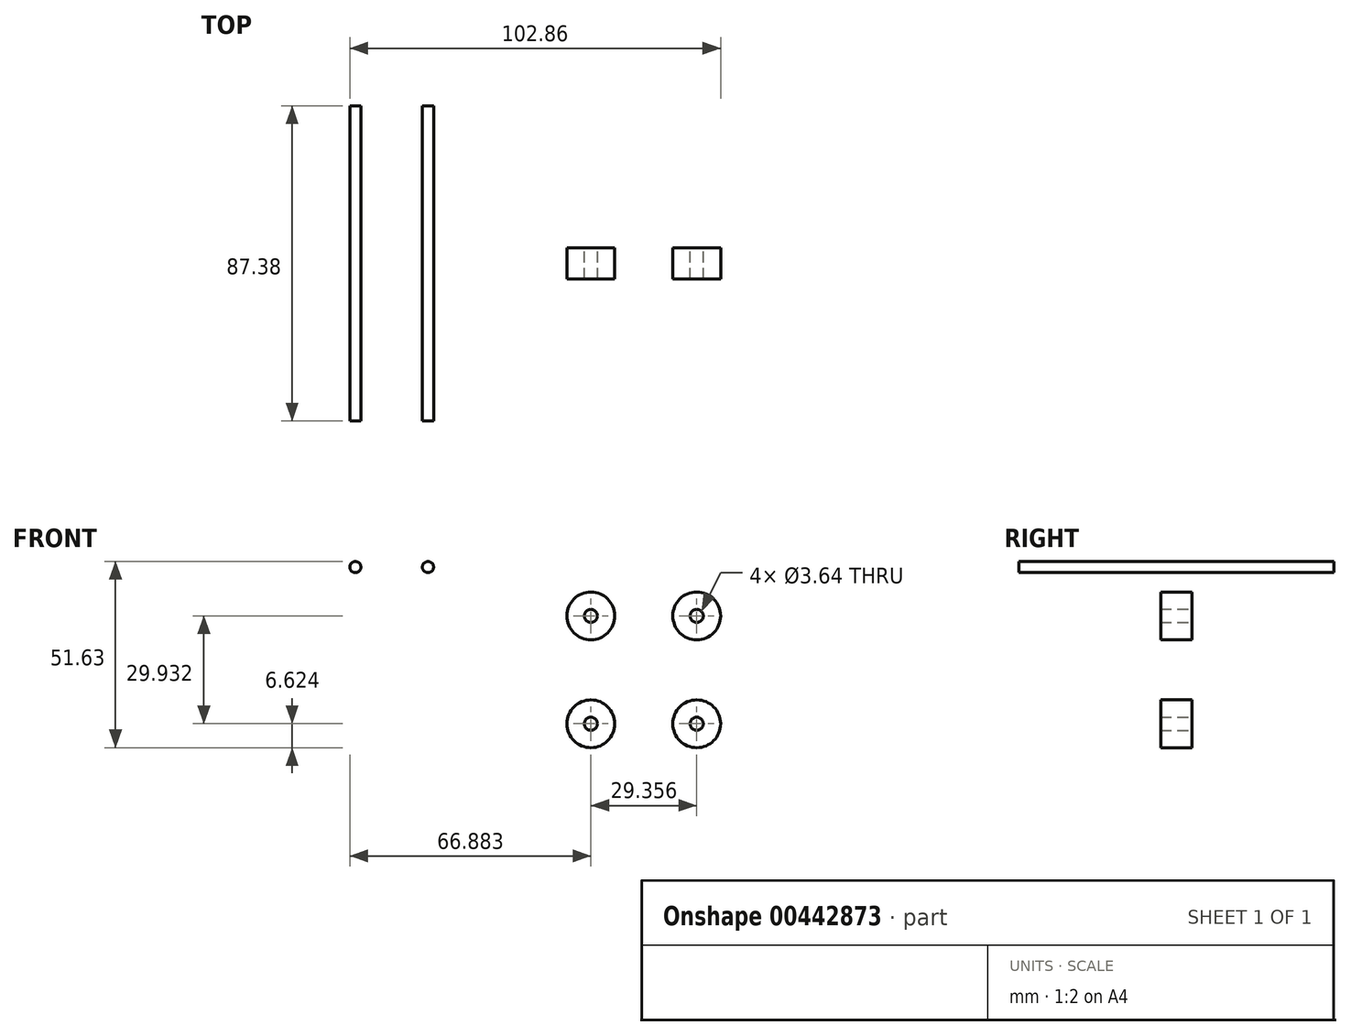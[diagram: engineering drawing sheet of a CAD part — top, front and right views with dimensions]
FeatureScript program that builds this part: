
annotation { "Feature Type Name" : "Feature", "Feature Type Description" : "" }
export const myFeature = defineFeature(function(context is Context, id is Id, definition is map)
    precondition{}
    {
        {
            var Q0;
            Q0=qCreatedBy(makeId("Front.planeOp"),FACE);
            var sketch = newSketch(context, id + "F0", { "sketchPlane" : qUnion([Q0])});
            skCircle(sketch, "E0", {"center": v(-48.64, 28.5) * mm, "radius": 1.55 * mm});
            skCircle(sketch, "E1", {"center": v(-28.5, 28.5) * mm, "radius": 1.55 * mm});
            skSolve(sketch);
        }
        {
            var Q0;
            Q0 = qSketchRegion(id + "F0", true);
            extrude(context, id + "F1", {"entities" : qUnion([Q0]), "endBound" : BoundingType.SYMMETRIC, "depth" : 87.38 * mm});
        }
        {
            var Q0;
            Q0=qCreatedBy(makeId("Front.planeOp"),FACE);
            var sketch = newSketch(context, id + "F2", { "sketchPlane" : qUnion([Q0])});
            skCircle(sketch, "E2", {"center": v(46.05, 14.97) * mm, "radius": 6.63 * mm});
            skCircle(sketch, "E3", {"center": v(46.05, 14.97) * mm, "radius": 1.82 * mm});
            skCircle(sketch, "E4.MirrorC", {"center": v(46.05, -14.97) * mm, "radius": 6.63 * mm});
            skCircle(sketch, "E5.MirrorC", {"center": v(46.05, -14.97) * mm, "radius": 1.82 * mm});
            skLineSegment(sketch, "E6", {"start": v(31.37, 26.2) * mm, "end": v(31.37, -34.54) * mm});
            skCircle(sketch, "E7.MirrorC", {"center": v(16.7, 14.97) * mm, "radius": 6.63 * mm});
            skCircle(sketch, "E8.MirrorC", {"center": v(16.7, 14.97) * mm, "radius": 1.82 * mm});
            skCircle(sketch, "E9.MirrorC", {"center": v(16.7, -14.97) * mm, "radius": 1.82 * mm});
            skCircle(sketch, "E10.MirrorC", {"center": v(16.7, -14.97) * mm, "radius": 6.63 * mm});
            skSolve(sketch);
        }
        {
            var Q0;
            Q0 = qSketchRegion(id + "F2", true);
            extrude(context, id + "F3", {"entities" : qUnion([Q0]), "endBound" : BoundingType.SYMMETRIC, "depth" : 8.64 * mm});
        }
    });
